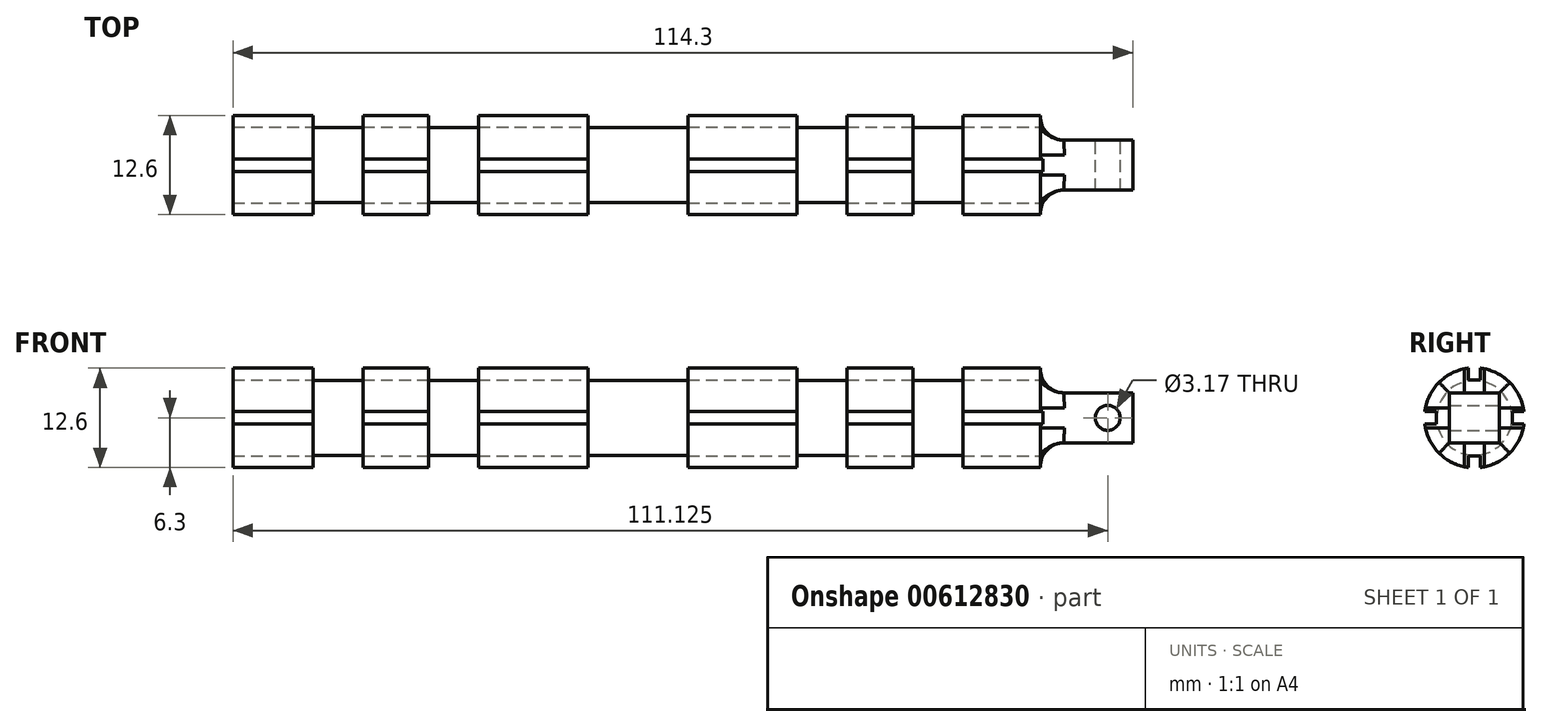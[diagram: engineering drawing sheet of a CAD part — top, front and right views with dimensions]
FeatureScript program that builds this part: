
annotation { "Feature Type Name" : "Feature", "Feature Type Description" : "" }
export const myFeature = defineFeature(function(context is Context, id is Id, definition is map)
    precondition{}
    {
        {
            var Q0;
            Q0=qCreatedBy(makeId("Front.planeOp"),FACE);
            var sketch = newSketch(context, id + "F0", { "sketchPlane" : qUnion([Q0])});
            skLineSegment(sketch, "E0", {"start": v(-57.15, 0) * mm, "end": v(57.15, 0) * mm});
            skLineSegment(sketch, "E1", {"start": v(57.15, 0) * mm, "end": v(57.15, 4.76) * mm});
            skLineSegment(sketch, "E2", {"start": v(45.4, 6.35) * mm, "end": v(35.56, 6.35) * mm});
            skLineSegment(sketch, "E3", {"start": v(35.56, 6.35) * mm, "end": v(35.56, 4.76) * mm});
            skLineSegment(sketch, "E4", {"start": v(35.56, 4.76) * mm, "end": v(29.21, 4.76) * mm});
            skLineSegment(sketch, "E5", {"start": v(29.21, 4.76) * mm, "end": v(29.21, 6.35) * mm});
            skLineSegment(sketch, "E6", {"start": v(29.21, 6.35) * mm, "end": v(20.88, 6.35) * mm});
            skLineSegment(sketch, "E7", {"start": v(20.88, 6.35) * mm, "end": v(20.88, 4.76) * mm});
            skLineSegment(sketch, "E8", {"start": v(20.88, 4.76) * mm, "end": v(14.53, 4.76) * mm});
            skLineSegment(sketch, "E9", {"start": v(14.53, 4.76) * mm, "end": v(14.53, 6.35) * mm});
            skLineSegment(sketch, "E10", {"start": v(14.53, 6.35) * mm, "end": v(0.63, 6.35) * mm});
            skLineSegment(sketch, "E11", {"start": v(0.63, 6.35) * mm, "end": v(0.63, 4.76) * mm});
            skLineSegment(sketch, "E12", {"start": v(0.63, 4.76) * mm, "end": v(-12.07, 4.76) * mm});
            skLineSegment(sketch, "E13", {"start": v(-12.07, 4.76) * mm, "end": v(-12.07, 6.35) * mm});
            skLineSegment(sketch, "E14", {"start": v(-12.07, 6.35) * mm, "end": v(-25.96, 6.35) * mm});
            skLineSegment(sketch, "E15", {"start": v(-25.96, 6.35) * mm, "end": v(-25.96, 4.76) * mm});
            skLineSegment(sketch, "E16", {"start": v(-25.96, 4.76) * mm, "end": v(-32.3, 4.76) * mm});
            skLineSegment(sketch, "E17", {"start": v(-32.3, 4.76) * mm, "end": v(-32.3, 6.35) * mm});
            skLineSegment(sketch, "E18", {"start": v(-32.3, 6.35) * mm, "end": v(-40.64, 6.35) * mm});
            skLineSegment(sketch, "E19", {"start": v(-40.64, 6.35) * mm, "end": v(-40.64, 4.76) * mm});
            skLineSegment(sketch, "E20", {"start": v(-40.64, 4.76) * mm, "end": v(-47, 4.76) * mm});
            skLineSegment(sketch, "E21", {"start": v(-47, 4.76) * mm, "end": v(-47, 6.35) * mm});
            skLineSegment(sketch, "E22", {"start": v(-47, 6.35) * mm, "end": v(-57.15, 6.35) * mm});
            skLineSegment(sketch, "E23", {"start": v(-57.15, 6.35) * mm, "end": v(-57.15, 0) * mm});
            skLineSegment(sketch, "E24", {"start": v(45.4, 6.35) * mm, "end": v(45.4, 4.76) * mm});
            skLineSegment(sketch, "E25", {"start": v(57.15, 4.76) * mm, "end": v(45.4, 4.76) * mm});
            skSolve(sketch);
        }
        {
            var Q0;
            Q0=qSketchRegion(id+"F0",true);
            var Q1;
            Q1=sQuery(id+"F0.wireOp",EDGE,"E0");
            revolve(context, id + "F1", {"entities" : qUnion([Q0]), "axis" : qUnion([Q1]), "revolveType" : RevolveType.FULL});
        }
        {
            var Q0;
            Q0=makeQuery(id+"F1.opRevolve","SWEPT_FACE",FACE,{"disambiguationData":[OSD([sQuery(id+"F0.wireOp",EDGE,"E1")])]});
            var sketch = newSketch(context, id + "F2", { "sketchPlane" : qUnion([Q0])});
            skCircle(sketch, "E26.0", {"center": v(0, 0) * mm, "radius": 4.76 * mm});
            skLineSegment(sketch, "E27.rect.bottom", {"start": v(-3.17, 3.18) * mm, "end": v(3.18, 3.18) * mm});
            skLineSegment(sketch, "E27.rect.top", {"start": v(-3.18, -3.18) * mm, "end": v(3.17, -3.18) * mm});
            skLineSegment(sketch, "E27.rect.left", {"start": v(-3.17, 3.18) * mm, "end": v(-3.18, -3.17) * mm});
            skLineSegment(sketch, "E27.rect.right", {"start": v(3.18, 3.18) * mm, "end": v(3.17, -3.18) * mm});
            skSolve(sketch);
        }
        {
            var Q0;
            Q0=qSketchRegion(id+"F2",true);
            extrude(context, id + "F3", {"entities" : qUnion([Q0]), "operationType" : NewBodyOperationType.REMOVE, "oppositeDirection" : true, "depth" : 11.75 * mm});
        }
        {
            var Q0;
            Q0=makeQuery(id+"F3.boolean.opBoolean","COPY",FACE,{"derivedFrom":makeQuery(id+"F3.opExtrude","SWEPT_FACE",FACE,{"disambiguationData":[OSD([sQuery(id+"F2.wireOp",EDGE,"E27.rect.left")])]})});
            var sketch = newSketch(context, id + "F4", { "sketchPlane" : qUnion([Q0])});
            skPoint(sketch, "E28", {"position": v(53.98, 0) * mm});
            skSolve(sketch);
        }
        {
            var Q0;
            Q0=sQuery(id+"F4.wireOp",VERTEX,"E28");
            var Q1;
            Q1=makeQuery(id+"F1.opRevolve","SWEPT_BODY",BODY,{"disambiguationData":[OSD([sQuery(id+"F0.wireOp",EDGE,"E0"),sQuery(id+"F0.wireOp",EDGE,"E1"),sQuery(id+"F0.wireOp",EDGE,"E2"),sQuery(id+"F0.wireOp",EDGE,"E3"),sQuery(id+"F0.wireOp",EDGE,"E4"),sQuery(id+"F0.wireOp",EDGE,"E5"),sQuery(id+"F0.wireOp",EDGE,"E6"),sQuery(id+"F0.wireOp",EDGE,"E7"),sQuery(id+"F0.wireOp",EDGE,"E8"),sQuery(id+"F0.wireOp",EDGE,"E9"),sQuery(id+"F0.wireOp",EDGE,"E10"),sQuery(id+"F0.wireOp",EDGE,"E11"),sQuery(id+"F0.wireOp",EDGE,"E12"),sQuery(id+"F0.wireOp",EDGE,"E13"),sQuery(id+"F0.wireOp",EDGE,"E14"),sQuery(id+"F0.wireOp",EDGE,"E15"),sQuery(id+"F0.wireOp",EDGE,"E16"),sQuery(id+"F0.wireOp",EDGE,"E17"),sQuery(id+"F0.wireOp",EDGE,"E18"),sQuery(id+"F0.wireOp",EDGE,"E19"),sQuery(id+"F0.wireOp",EDGE,"E20"),sQuery(id+"F0.wireOp",EDGE,"E21"),sQuery(id+"F0.wireOp",EDGE,"E22"),sQuery(id+"F0.wireOp",EDGE,"E23"),sQuery(id+"F0.wireOp",EDGE,"E24"),sQuery(id+"F0.wireOp",EDGE,"E25")])]});
            hole(context, id + "F5", {"style" : HoleStyle.SIMPLE, "holeDiameter" : 3.17 * mm, "endStyle" : HoleEndStyle.THROUGH, "locations" : qUnion([Q0]), "scope" : qUnion([Q1])});
        }
        {
            var Q0;
            Q0=makeQuery(id+"F3.boolean.opBoolean","COPY",EDGE,{"derivedFrom":makeQuery(id+"F3.opExtrude","CAP_EDGE",EDGE,{"disambiguationData":[OSD([sQuery(id+"F2.wireOp",EDGE,"E27.rect.bottom")])],"isStart":false})});
            var Q1;
            Q1=makeQuery(id+"F3.boolean.opBoolean","COPY",EDGE,{"derivedFrom":makeQuery(id+"F3.opExtrude","CAP_EDGE",EDGE,{"disambiguationData":[OSD([sQuery(id+"F2.wireOp",EDGE,"E27.rect.left")])],"isStart":false})});
            var Q2;
            Q2=makeQuery(id+"F3.boolean.opBoolean","COPY",EDGE,{"derivedFrom":makeQuery(id+"F3.opExtrude","CAP_EDGE",EDGE,{"disambiguationData":[OSD([sQuery(id+"F2.wireOp",EDGE,"E27.rect.top")])],"isStart":false})});
            var Q3;
            Q3=makeQuery(id+"F3.boolean.opBoolean","COPY",EDGE,{"derivedFrom":makeQuery(id+"F3.opExtrude","CAP_EDGE",EDGE,{"disambiguationData":[OSD([sQuery(id+"F2.wireOp",EDGE,"E27.rect.right")])],"isStart":false})});
            fillet(context, id + "F6", {"entities" : qUnion([Q0, Q1, Q2, Q3]), "radius" : 3.05 * mm, "tangentPropagation" : true, "allowEdgeOverflow" : false});
        }
        {
            var Q0;
            Q0=qCreatedBy(makeId("Right.planeOp"),FACE);
            var sketch = newSketch(context, id + "F7", { "sketchPlane" : qUnion([Q0])});
            skLineSegment(sketch, "E29.rect.bottom", {"start": v(-0.79, 6.35) * mm, "end": v(0.79, 6.35) * mm});
            skLineSegment(sketch, "E29.rect.top", {"start": v(-0.79, 4.83) * mm, "end": v(0.79, 4.83) * mm});
            skLineSegment(sketch, "E29.rect.left", {"start": v(-0.79, 6.35) * mm, "end": v(-0.79, 4.83) * mm});
            skLineSegment(sketch, "E29.rect.right", {"start": v(0.79, 6.35) * mm, "end": v(0.79, 4.83) * mm});
            skPoint(sketch, "E29.rect.middle", {"position": v(0, 5.59) * mm});
            skLineSegment(sketch, "E30.rect.bottom", {"start": v(-4.83, -0.79) * mm, "end": v(-6.35, -0.79) * mm});
            skLineSegment(sketch, "E30.rect.top", {"start": v(-4.83, 0.79) * mm, "end": v(-6.35, 0.79) * mm});
            skLineSegment(sketch, "E30.rect.left", {"start": v(-4.83, -0.79) * mm, "end": v(-4.83, 0.79) * mm});
            skLineSegment(sketch, "E30.rect.right", {"start": v(-6.35, -0.79) * mm, "end": v(-6.35, 0.79) * mm});
            skPoint(sketch, "E30.rect.middle", {"position": v(-5.59, 0) * mm});
            skLineSegment(sketch, "E31.rect.bottom", {"start": v(6.35, -0.79) * mm, "end": v(4.83, -0.79) * mm});
            skLineSegment(sketch, "E31.rect.top", {"start": v(6.35, 0.79) * mm, "end": v(4.83, 0.79) * mm});
            skLineSegment(sketch, "E31.rect.left", {"start": v(6.35, -0.79) * mm, "end": v(6.35, 0.79) * mm});
            skLineSegment(sketch, "E31.rect.right", {"start": v(4.83, -0.79) * mm, "end": v(4.83, 0.79) * mm});
            skPoint(sketch, "E31.rect.middle", {"position": v(5.59, 0) * mm});
            skLineSegment(sketch, "E32.rect.bottom", {"start": v(0.79, -6.35) * mm, "end": v(-0.79, -6.35) * mm});
            skLineSegment(sketch, "E32.rect.top", {"start": v(0.79, -4.83) * mm, "end": v(-0.79, -4.83) * mm});
            skLineSegment(sketch, "E32.rect.left", {"start": v(0.79, -6.35) * mm, "end": v(0.79, -4.83) * mm});
            skLineSegment(sketch, "E32.rect.right", {"start": v(-0.79, -6.35) * mm, "end": v(-0.79, -4.83) * mm});
            skPoint(sketch, "E32.rect.middle", {"position": v(0, -5.59) * mm});
            skSolve(sketch);
        }
        {
            var Q0;
            Q0=qSketchRegion(id+"F7",true);
            extrude(context, id + "F8", {"entities" : qUnion([Q0]), "operationType" : NewBodyOperationType.REMOVE, "oppositeDirection" : true, "depth" : 127 * mm, "symmetric" : true});
        }
    });
